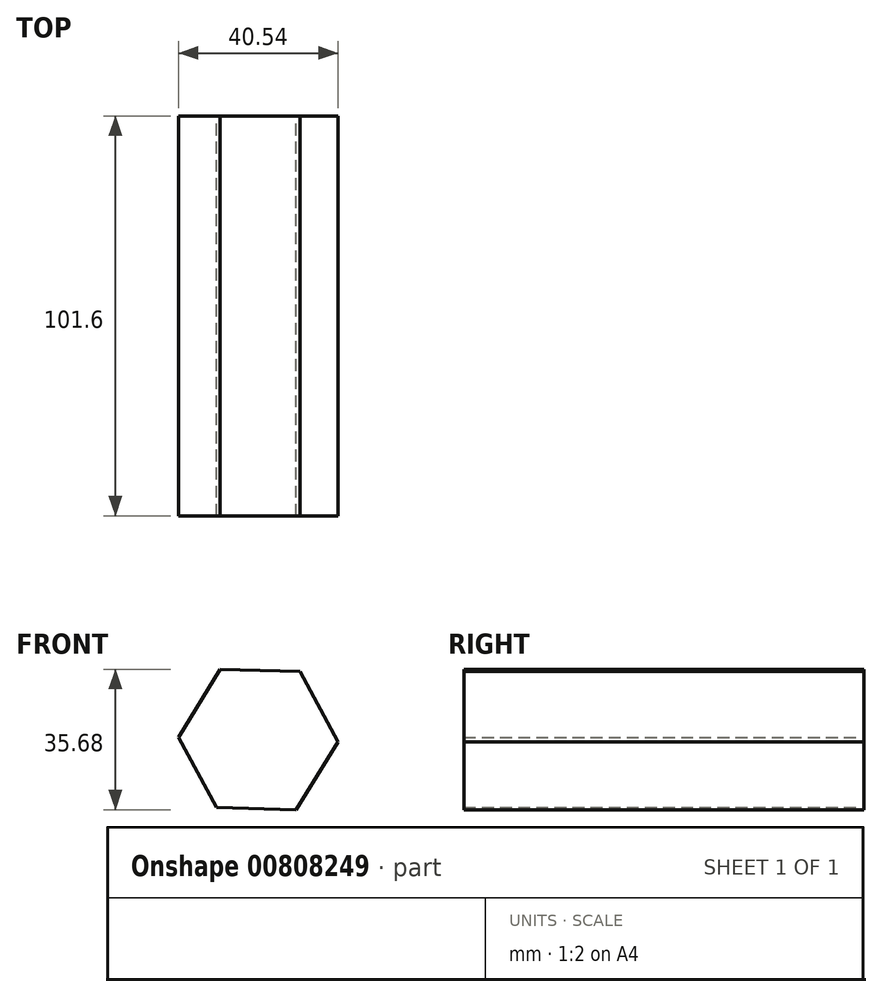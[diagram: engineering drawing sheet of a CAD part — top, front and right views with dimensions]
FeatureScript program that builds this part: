
annotation { "Feature Type Name" : "Feature", "Feature Type Description" : "" }
export const myFeature = defineFeature(function(context is Context, id is Id, definition is map)
    precondition{}
    {
        {
            var Q0;
            Q0=qCreatedBy(makeId("Front.planeOp"),FACE);
            var sketch = newSketch(context, id + "F0", { "sketchPlane" : qUnion([Q0])});
            skCircle(sketch, "E0.cCircle", {"center": v(0, 0) * mm, "radius": 17.56 * mm, "construction": true});
            skLineSegment(sketch, "E0.0", {"start": v(20.27, -0.56) * mm, "end": v(9.65, -17.84) * mm});
            skLineSegment(sketch, "E0.1", {"start": v(9.65, -17.84) * mm, "end": v(-10.62, -17.27) * mm});
            skLineSegment(sketch, "E0.2", {"start": v(-10.62, -17.27) * mm, "end": v(-20.27, 0.56) * mm});
            skLineSegment(sketch, "E0.3", {"start": v(-20.27, 0.56) * mm, "end": v(-9.65, 17.84) * mm});
            skLineSegment(sketch, "E0.4", {"start": v(-9.65, 17.84) * mm, "end": v(10.62, 17.27) * mm});
            skLineSegment(sketch, "E0.5", {"start": v(10.62, 17.27) * mm, "end": v(20.27, -0.56) * mm});
            skPoint(sketch, "E0.0.midPoint", {"position": v(14.96, -9.2) * mm});
            skSolve(sketch);
        }
        {
            var Q0;
            Q0 = qSketchRegion(id + "F0", true);
            extrude(context, id + "F1", {"entities" : qUnion([Q0]), "depth" : 101.6 * mm, "offsetDistance" : 25.4 * mm});
        }
        {
            var Q0;
            Q0=makeQuery(id+"F1.opExtrude","CAP_FACE",FACE,{"disambiguationData":[OSD([sQuery(id+"F0.wireOp",EDGE,"E0.0"),sQuery(id+"F0.wireOp",EDGE,"E0.1"),sQuery(id+"F0.wireOp",EDGE,"E0.2"),sQuery(id+"F0.wireOp",EDGE,"E0.3"),sQuery(id+"F0.wireOp",EDGE,"E0.4"),sQuery(id+"F0.wireOp",EDGE,"E0.5")])],"isStart":false});
            shell(context, id + "F2", {"entities" : qUnion([Q0]), "thickness" : 889 * mm});
        }
    });
